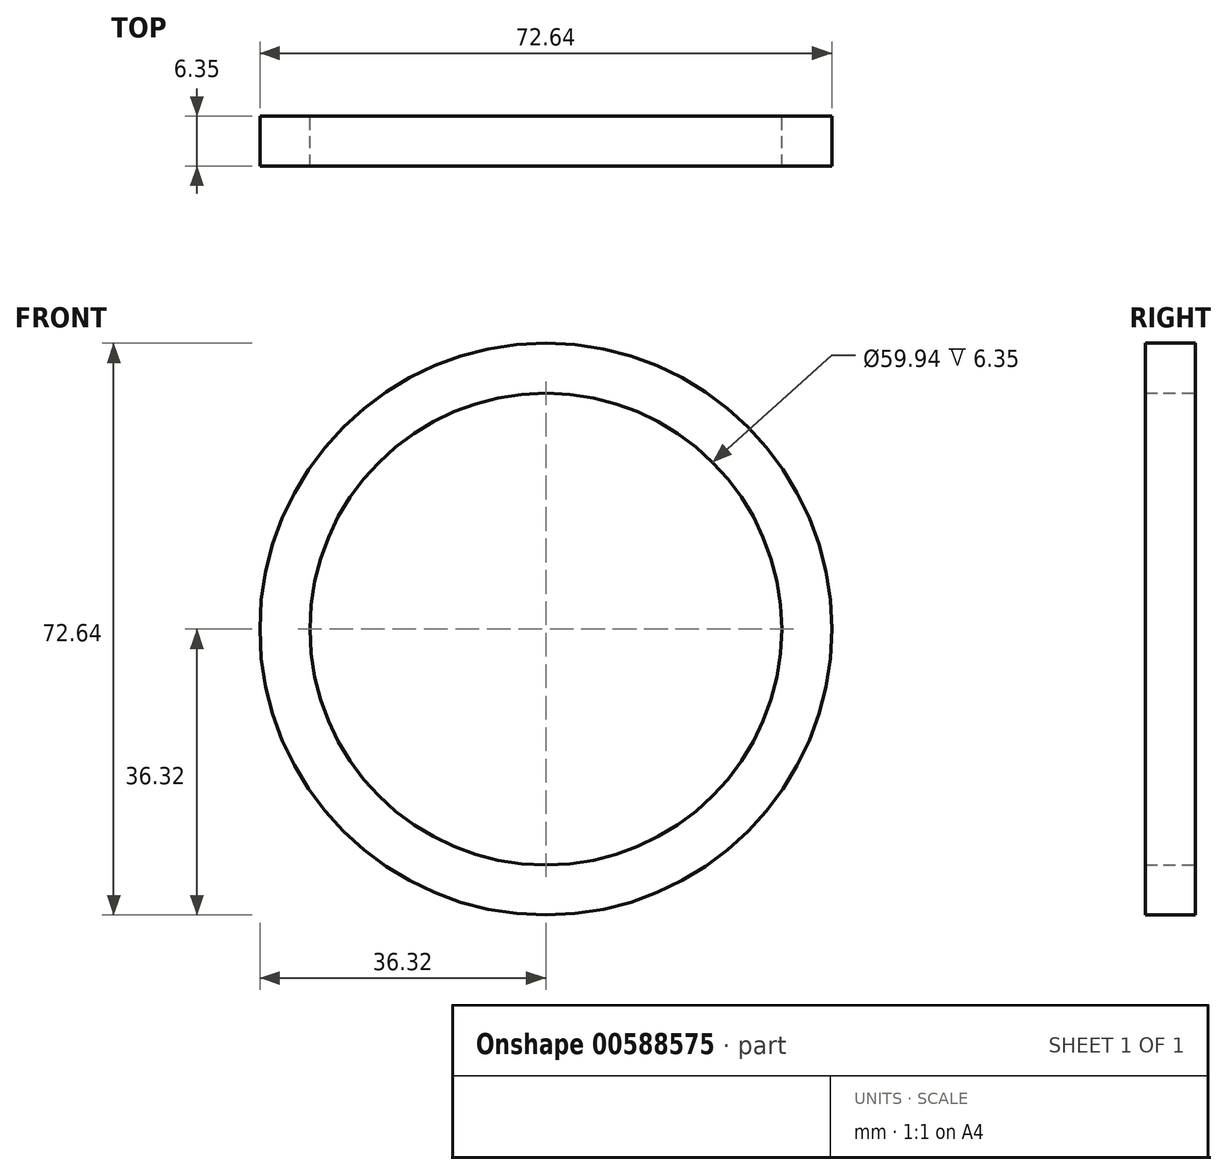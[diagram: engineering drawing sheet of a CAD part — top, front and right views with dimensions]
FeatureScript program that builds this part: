
annotation { "Feature Type Name" : "Feature", "Feature Type Description" : "" }
export const myFeature = defineFeature(function(context is Context, id is Id, definition is map)
    precondition{}
    {
        {
            var Q0;
            Q0=qCreatedBy(makeId("Front.planeOp"),FACE);
            var sketch = newSketch(context, id + "F0", { "sketchPlane" : qUnion([Q0])});
            skCircle(sketch, "E0", {"center": v(0, 0) * mm, "radius": 36.32 * mm});
            skCircle(sketch, "E1.0", {"center": v(0, 0) * mm, "radius": 29.97 * mm});
            skSolve(sketch);
        }
        {
            var Q0;
            Q0 = qSketchRegion(id + "F0", true);
            var Q1;
            Q1=makeQuery(id+"F0.imprint","IMPRINT",FACE,{"disambiguationData":[TD([[makeQuery(id+"F0.imprint","IMPRINT",EDGE,{"derivedFrom":sQuery(id+"F0.wireOp",EDGE,"E0")}),1.0]])]});
            extrude(context, id + "F1", {"entities" : qUnion([Q0, Q1]), "depth" : 6.35 * mm, "offsetDistance" : 25.4 * mm});
        }
    });
